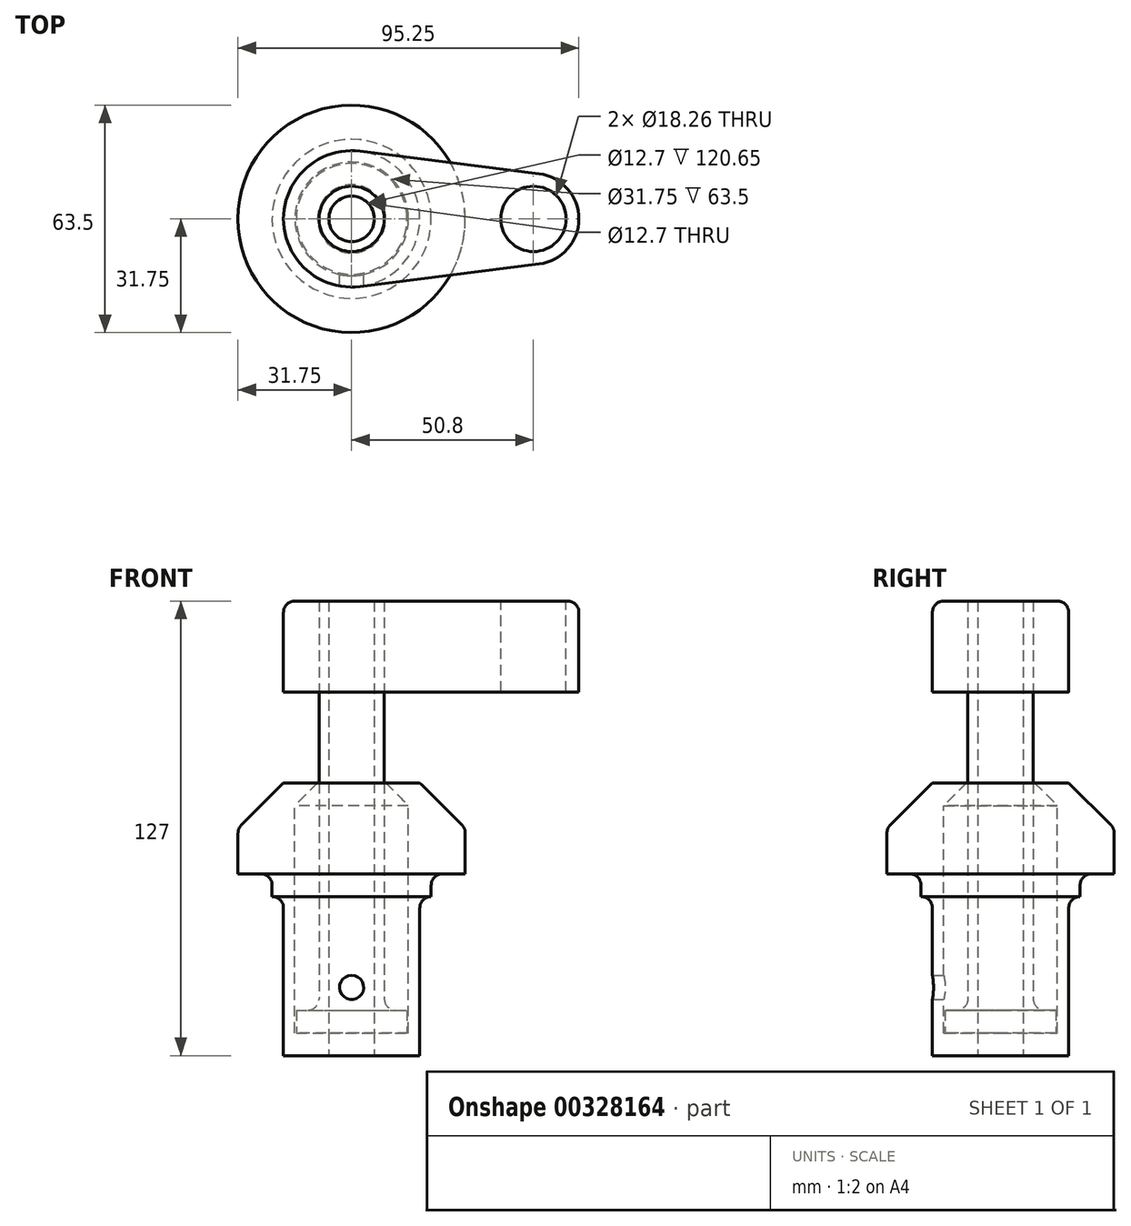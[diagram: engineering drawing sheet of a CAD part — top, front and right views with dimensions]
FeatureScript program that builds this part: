
annotation { "Feature Type Name" : "Feature", "Feature Type Description" : "" }
export const myFeature = defineFeature(function(context is Context, id is Id, definition is map)
    precondition{}
    {
        {
            var Q0;
            Q0=qCreatedBy(makeId("Front.planeOp"),FACE);
            var sketch = newSketch(context, id + "F0", { "sketchPlane" : qUnion([Q0])});
            skLineSegment(sketch, "E0", {"start": v(0, 0) * mm, "end": v(19.05, 0) * mm});
            skLineSegment(sketch, "E1", {"start": v(19.05, 0) * mm, "end": v(19.05, 44.45) * mm});
            skLineSegment(sketch, "E2", {"start": v(19.05, 44.45) * mm, "end": v(22.23, 44.45) * mm});
            skLineSegment(sketch, "E3", {"start": v(22.23, 44.45) * mm, "end": v(22.23, 50.8) * mm});
            skLineSegment(sketch, "E4", {"start": v(22.23, 50.8) * mm, "end": v(31.75, 50.8) * mm});
            skLineSegment(sketch, "E5", {"start": v(31.75, 50.8) * mm, "end": v(31.75, 63.5) * mm});
            skLineSegment(sketch, "E6", {"start": v(31.75, 63.5) * mm, "end": v(19.05, 76.2) * mm});
            skLineSegment(sketch, "E7", {"start": v(19.05, 76.2) * mm, "end": v(0, 76.2) * mm});
            skLineSegment(sketch, "E8", {"start": v(0, 76.2) * mm, "end": v(0, 0) * mm});
            skLineSegment(sketch, "E9", {"start": v(9.52, 76.2) * mm, "end": v(15.87, 69.85) * mm});
            skLineSegment(sketch, "E10", {"start": v(15.87, 69.85) * mm, "end": v(15.88, 6.35) * mm});
            skLineSegment(sketch, "E11", {"start": v(15.88, 6.35) * mm, "end": v(0, 6.35) * mm});
            skLineSegment(sketch, "E12", {"start": v(0, 76.2) * mm, "end": v(0, 92.83) * mm, "construction": true});
            skLineSegment(sketch, "E13", {"start": v(0, 76.2) * mm, "end": v(0, 127) * mm});
            skLineSegment(sketch, "E14", {"start": v(0, 127) * mm, "end": v(9.13, 127) * mm});
            skLineSegment(sketch, "E15", {"start": v(9.13, 127) * mm, "end": v(9.13, 12.7) * mm});
            skLineSegment(sketch, "E16", {"start": v(9.13, 12.7) * mm, "end": v(15.48, 12.7) * mm});
            skLineSegment(sketch, "E17", {"start": v(15.48, 12.7) * mm, "end": v(15.48, 6.35) * mm});
            skSolve(sketch);
        }
        {
            var Q0;
            {var subQ4=sQuery(id+"F0.wireOp",EDGE,"E0");Q0=makeQuery(id+"F0.imprint","IMPRINT",FACE,{"disambiguationData":[TD([[makeQuery(id+"F0.imprint","IMPRINT",EDGE,{"derivedFrom":subQ4}),1.0]])]});}
            var Q1;
            Q1=sQuery(id+"F0.wireOp",EDGE,"E8");
            revolve(context, id + "F1", {"entities" : qUnion([Q0]), "axis" : qUnion([Q1]), "revolveType" : RevolveType.FULL});
        }
        {
            var Q0;
            {var subQ0=sQuery(id+"F0.wireOp",EDGE,"E13");Q0=makeQuery(id+"F0.imprint","IMPRINT",FACE,{"disambiguationData":[TD([[makeQuery(id+"F0.imprint","IMPRINT",EDGE,{"derivedFrom":subQ0}),-1.0]])]});}
            var Q1;
            {var subQ6=sQuery(id+"F0.wireOp",EDGE,"E16");Q1=makeQuery(id+"F0.imprint","IMPRINT",FACE,{"disambiguationData":[TD([[makeQuery(id+"F0.imprint","IMPRINT",EDGE,{"derivedFrom":subQ6}),-1.0]])]});}
            var Q2;
            Q2=sQuery(id+"F0.wireOp",EDGE,"E13");
            revolve(context, id + "F2", {"entities" : qUnion([Q0, Q1]), "axis" : qUnion([Q2]), "revolveType" : RevolveType.FULL});
        }
        {
            var Q0;
            Q0=makeQuery(id+"F2.opRevolve","SWEPT_FACE",FACE,{"disambiguationData":[OSD([sQuery(id+"F0.wireOp",EDGE,"E14")])]});
            var sketch = newSketch(context, id + "F3", { "sketchPlane" : qUnion([Q0])});
            skCircle(sketch, "E18.0", {"center": v(0, 0) * mm, "radius": 9.13 * mm});
            skCircle(sketch, "E19", {"center": v(0, 0) * mm, "radius": 19.05 * mm});
            skCircle(sketch, "E20", {"center": v(50.8, 0) * mm, "radius": 12.7 * mm});
            skLineSegment(sketch, "E21", {"start": v(52.39, 12.6) * mm, "end": v(2.38, 18.9) * mm});
            skLineSegment(sketch, "E22", {"start": v(52.39, -12.6) * mm, "end": v(2.38, -18.9) * mm});
            skCircle(sketch, "E23", {"center": v(50.8, 0) * mm, "radius": 9.13 * mm});
            skSolve(sketch);
        }
        {
            var Q0;
            Q0=makeQuery(id+"F3.imprint","IMPRINT",FACE,{"disambiguationData":[TD([[makeQuery(id+"F3.imprint","IMPRINT",EDGE,{"derivedFrom":sQuery(id+"F3.wireOp",EDGE,"E18.0")}),1.0]])]});
            var Q1;
            {var subQ0=sQuery(id+"F3.wireOp",EDGE,"E21");Q1=makeQuery(id+"F3.imprint","IMPRINT",FACE,{"disambiguationData":[TD([[makeQuery(id+"F3.imprint","IMPRINT",EDGE,{"derivedFrom":subQ0}),1.0]])]});}
            var Q2;
            Q2=makeQuery(id+"F3.imprint","IMPRINT",FACE,{"disambiguationData":[TD([[makeQuery(id+"F3.imprint","IMPRINT",EDGE,{"derivedFrom":sQuery(id+"F3.wireOp",EDGE,"E23")}),-1.0]])]});
            var Q3;
            Q3=makeQuery(id+"F1.opRevolve","SWEPT_FACE",FACE,{"disambiguationData":[OSD([sQuery(id+"F0.wireOp",EDGE,"E7")])]});
            extrude(context, id + "F4", {"entities" : qUnion([Q0, Q1, Q2]), "oppositeDirection" : true, "endBoundEntityFace" : qUnion([Q3]), "depth" : 25.4 * mm});
        }
        {
            var Q0;
            Q0=qCreatedBy(makeId("Front.planeOp"),FACE);
            var sketch = newSketch(context, id + "F5", { "sketchPlane" : qUnion([Q0])});
            skPoint(sketch, "E24", {"position": v(0, 19.05) * mm});
            skSolve(sketch);
        }
        {
            var Q0;
            Q0=sQuery(id+"F5.wireOp",VERTEX,"E24");
            var Q1;
            Q1=makeQuery(id+"F1.opRevolve","SWEPT_BODY",BODY,{"disambiguationData":[OSD([sQuery(id+"F0.wireOp",EDGE,"E0"),sQuery(id+"F0.wireOp",EDGE,"E1"),sQuery(id+"F0.wireOp",EDGE,"E2"),sQuery(id+"F0.wireOp",EDGE,"E3"),sQuery(id+"F0.wireOp",EDGE,"E4"),sQuery(id+"F0.wireOp",EDGE,"E5"),sQuery(id+"F0.wireOp",EDGE,"E6"),sQuery(id+"F0.wireOp",EDGE,"E7"),sQuery(id+"F0.wireOp",EDGE,"E8"),sQuery(id+"F0.wireOp",EDGE,"E9"),sQuery(id+"F0.wireOp",EDGE,"E10"),sQuery(id+"F0.wireOp",EDGE,"E11")])]});
            hole(context, id + "F6", {"style" : HoleStyle.SIMPLE, "endStyle" : HoleEndStyle.THROUGH, "oppositeDirection" : true, "standardTappedOrClearance" : lookupTablePath({ "standard" : "ANSI", "fit" : "Normal (ASME)", "size" : "1/4", "type" : "Clearance" }), "standardBlindInLast" : lookupTablePath({ "fit" : "Free", "standard" : "ANSI", "size" : "1/4", "type" : "Clearance" }), "holeDiameter" : 6.76 * mm, "tappedDepth" : 13.2 * mm, "tapClearance" : 3, "locations" : qUnion([Q0]), "scope" : qUnion([Q1])});
        }
        {
            var Q0;
            Q0=makeQuery(id+"F4.opExtrude","CAP_EDGE",EDGE,{"disambiguationData":[OSD([sQuery(id+"F3.wireOp",EDGE,"E22")])],"isStart":true});
            var Q1;
            Q1=makeQuery(id+"F1.opRevolve","SWEPT_EDGE",EDGE,{"disambiguationData":[OSD([sQuery(id+"F0.wireOp",EDGE,"E5"),sQuery(id+"F0.wireOp",EDGE,"E6")])]});
            var Q2;
            Q2=makeQuery(id+"F1.opRevolve","SWEPT_EDGE",EDGE,{"disambiguationData":[OSD([sQuery(id+"F0.wireOp",EDGE,"E3"),sQuery(id+"F0.wireOp",EDGE,"E4")])]});
            var Q3;
            Q3=makeQuery(id+"F1.opRevolve","SWEPT_EDGE",EDGE,{"disambiguationData":[OSD([sQuery(id+"F0.wireOp",EDGE,"E1"),sQuery(id+"F0.wireOp",EDGE,"E2")])]});
            var Q4;
            Q4=makeQuery(id+"F2.opRevolve","SWEPT_EDGE",EDGE,{"disambiguationData":[OSD([sQuery(id+"F0.wireOp",EDGE,"E15"),sQuery(id+"F0.wireOp",EDGE,"E16")])]});
            fillet(context, id + "F7", {"entities" : qUnion([Q0, Q1, Q2, Q3, Q4]), "radius" : 3.17 * mm, "tangentPropagation" : true, "allowEdgeOverflow" : false});
        }
        {
            var Q0;
            Q0=makeQuery(id+"F1.opRevolve","SWEPT_FACE",FACE,{"disambiguationData":[OSD([sQuery(id+"F0.wireOp",EDGE,"E0")])]});
            var sketch = newSketch(context, id + "F8", { "sketchPlane" : qUnion([Q0])});
            skCircle(sketch, "E25", {"center": v(0, 0) * mm, "radius": 6.35 * mm});
            skSolve(sketch);
        }
        {
            var Q0;
            Q0 = qSketchRegion(id + "F8", true);
            extrude(context, id + "F9", {"entities" : qUnion([Q0]), "operationType" : NewBodyOperationType.REMOVE, "endBound" : BoundingType.THROUGH_ALL, "oppositeDirection" : true, "depth" : 25.4 * mm});
        }
    });
